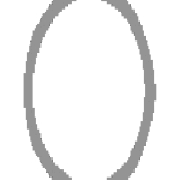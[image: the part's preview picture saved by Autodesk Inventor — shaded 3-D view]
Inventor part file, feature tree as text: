
AUTODESK INVENTOR PART (.ipt)
format: ipt  version: 2021 (Build 250183000, 183)  size: 155,648 bytes
history: native  units: in
note: dims shown in document units (in); Inventor stores cm internally (conversion verified against a paired STEP export)
features: plane x10, sketch x6, other x4, extrude x3, boolean_combine x3
ambient origin geometry x8: Origin, YZ Plane, XZ Plane, XY Plane, X Axis, Y Axis, Z Axis, Center Point
bodies: Solid1 (feature_tree), Body (feature_tree), Solid2 (feature_tree), Solid3 (feature_tree), Solid4 (feature_tree)
feature tree (26):
  other  "Driven Length"
  other  "Frame Generator"
  other  "Start Plane"
  other  "End Plane"
  plane  "Work Plane4"
  plane  "Work Plane5"
  plane  "Work Plane6"
  extrude  "Extrusion3"  Depth=0.065in
  boolean_combine  "Combine1"
  plane  "Work Plane7"
  plane  "Work Plane8"
  plane  "Work Plane9"
  extrude  "Extrusion4"  TaperAngle=0.0deg  [1 undecoded]
  boolean_combine  "Combine2"
  plane  "Work Plane10"
  plane  "Work Plane11"
  plane  "Work Plane12"
  extrude  "Extrusion5"  Depth=0.12in TaperAngle=0.0deg
  boolean_combine  "Combine3"
  sketch  "Sketch"  dims[d10=0.12in d11=0.0in d12=0.12in d13=0.0in d14=0.12in d15=0.0in]
  sketch  "Sketch2"  dims[d0=1.0in d1=0.065in]
  plane  "Work Plane3"
  sketch  "Sketch3"  dims[d2=12.431in d4=-0.0in]
  sketch  "Sketch4"  dims[d5=12.431in d6=0.12in d7=0.0in]
  sketch  "Sketch5"  dims[d8=90.0deg]
  sketch  "Sketch6"  dims[d9=12.431in]
note: 1 required parameter value undecoded (feature->parameter linkage not recoverable at this tier; creation-order binding heuristic only, values carry confidence <= 0.55)
